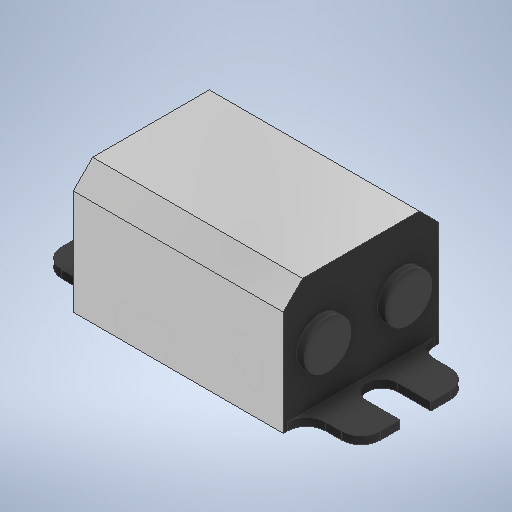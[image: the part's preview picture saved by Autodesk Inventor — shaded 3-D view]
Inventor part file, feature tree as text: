
AUTODESK INVENTOR PART (.ipt)
format: ipt  version: 2025 (Build 290162000, 162)  size: 303,616 bytes
history: native  units: in
note: dims shown in document units (in); Inventor stores cm internally (conversion verified against a paired STEP export)
features: extrude x3, sketch x3, mirror x2, projected_geometry x2, plane x1, chamfer x1
ambient origin geometry x8: Origin, YZ Plane, XZ Plane, XY Plane, X Axis, Y Axis, Z Axis, Center Point
bodies: Solid1 (feature_tree), Solid2 (feature_tree), Solid3 (feature_tree)
feature tree (12):
  extrude  "Extrusion1"  Depth=1.0in
  sketch  "Sketch2"  dims[d2=0.8in d3=0.0in d4=0.3in]
  plane  "Work Plane1"
  extrude  "Extrusion2"  Depth=0.3in
  mirror  "Mirror1"
  extrude  "Extrusion3"  Depth=0.05in TaperAngle=0.0deg
  mirror  "Mirror2"
  chamfer  "Chamfer1"  Distance=0.075in
  sketch  "Sketch1"  dims[d0=1.35in d1=1.0in]
  projected_geometry  "Projected Loop1"
  sketch  "Sketch3"  dims[d5=0.3in d6=0.05in d7=0.0in d8=0.075in d9=0.2in d10=0.35in d11=0.25in d12=0.125in d13=0.1in d14=0.125in d15=0.125in d16=0.05in d17=0.0in d18=0.125in d19=0.125in d20=45.0deg]
  projected_geometry  "Projected Loop2"
